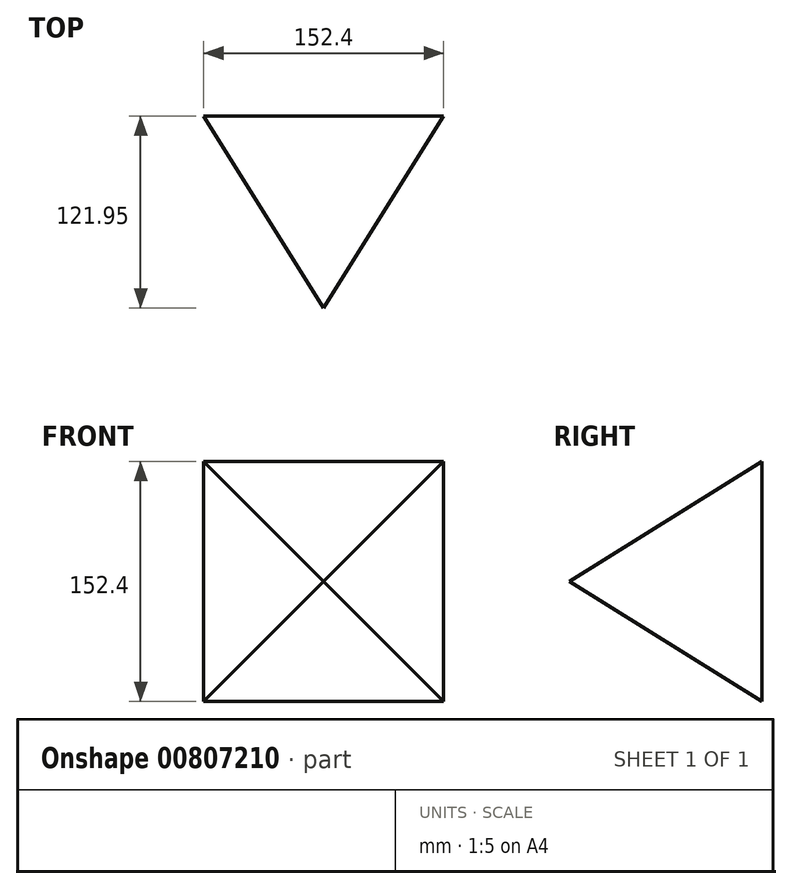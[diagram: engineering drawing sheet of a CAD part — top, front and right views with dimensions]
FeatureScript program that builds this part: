
annotation { "Feature Type Name" : "Feature", "Feature Type Description" : "" }
export const myFeature = defineFeature(function(context is Context, id is Id, definition is map)
    precondition{}
    {
        {
            var Q0;
            Q0=qCreatedBy(makeId("Front.planeOp"),FACE);
            var sketch = newSketch(context, id + "F0", { "sketchPlane" : qUnion([Q0])});
            skLineSegment(sketch, "E0.bottom", {"start": v(-74.34, 66.4) * mm, "end": v(78.06, 66.4) * mm});
            skLineSegment(sketch, "E0.top", {"start": v(-74.34, -86) * mm, "end": v(78.06, -86) * mm});
            skLineSegment(sketch, "E0.left", {"start": v(-74.34, 66.4) * mm, "end": v(-74.34, -86) * mm});
            skLineSegment(sketch, "E0.right", {"start": v(78.06, 66.4) * mm, "end": v(78.06, -86) * mm});
            skSolve(sketch);
        }
        {
            var Q0;
            Q0=makeQuery(id+"F0.imprint","IMPRINT",FACE,{"disambiguationData":[TD([[makeQuery(id+"F0.imprint","IMPRINT",EDGE,{"derivedFrom":sQuery(id+"F0.wireOp",EDGE,"E0.bottom")}),-1.0]])]});
            extrude(context, id + "F1", {"entities" : qUnion([Q0]), "depth" : 152.15 * mm, "offsetDistance" : 25.4 * mm, "hasDraft" : true, "draftAngle" : 32 * degree, "draftPullDirection" : true});
        }
    });
